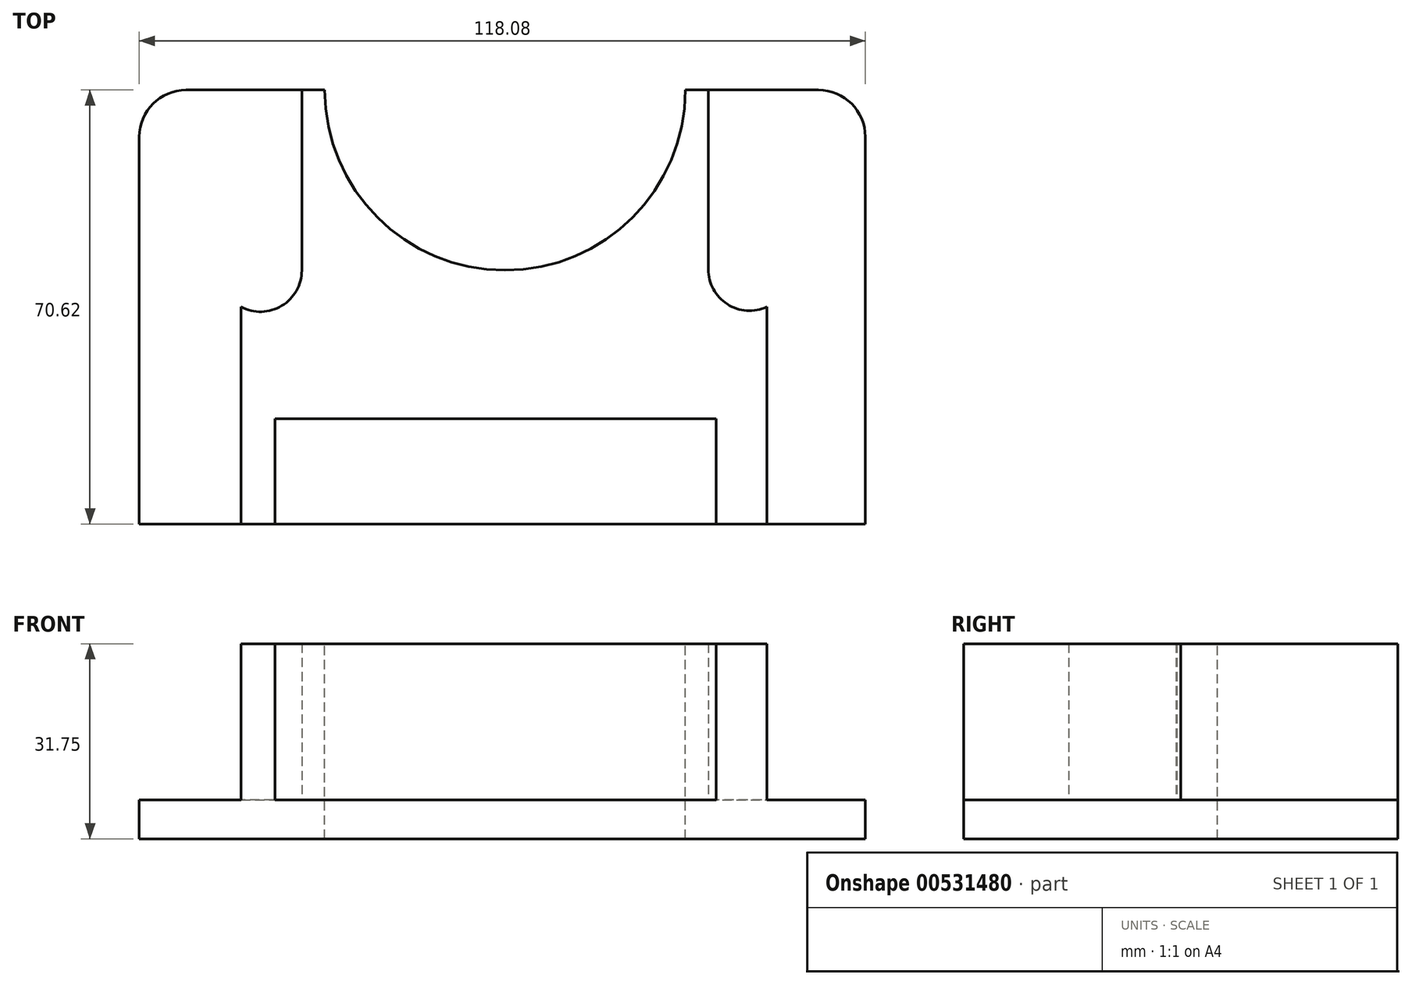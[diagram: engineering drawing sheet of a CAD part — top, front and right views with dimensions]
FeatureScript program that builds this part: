
annotation { "Feature Type Name" : "Feature", "Feature Type Description" : "" }
export const myFeature = defineFeature(function(context is Context, id is Id, definition is map)
    precondition{}
    {
        {
            var Q0;
            Q0=qCreatedBy(makeId("Top.planeOp"),FACE);
            var sketch = newSketch(context, id + "F0", { "sketchPlane" : qUnion([Q0])});
            skLineSegment(sketch, "E0.bottom", {"start": v(59.04, 35.31) * mm, "end": v(-59.04, 35.31) * mm});
            skLineSegment(sketch, "E0.top", {"start": v(59.04, -35.31) * mm, "end": v(-59.04, -35.31) * mm});
            skLineSegment(sketch, "E0.left", {"start": v(59.04, 35.31) * mm, "end": v(59.04, -35.31) * mm});
            skLineSegment(sketch, "E0.right", {"start": v(-59.04, 35.31) * mm, "end": v(-59.04, -35.31) * mm});
            skPoint(sketch, "E0.middle", {"position": v(0, 0) * mm});
            skSolve(sketch);
        }
        {
            var Q0;
            Q0=makeQuery(id+"F0.imprint","IMPRINT",FACE,{"disambiguationData":[TD([[makeQuery(id+"F0.imprint","IMPRINT",EDGE,{"derivedFrom":sQuery(id+"F0.wireOp",EDGE,"E0.bottom")}),1.0]])]});
            extrude(context, id + "F1", {"entities" : qUnion([Q0]), "depth" : 6.35 * mm, "offsetDistance" : 25.4 * mm});
        }
        {
            var Q0;
            Q0=makeQuery(id+"F1.opExtrude","SWEPT_EDGE",EDGE,{"disambiguationData":[OSD([sQuery(id+"F0.wireOp",EDGE,"E0.bottom"),sQuery(id+"F0.wireOp",EDGE,"E0.right")])]});
            var Q1;
            Q1=makeQuery(id+"F1.opExtrude","SWEPT_EDGE",EDGE,{"disambiguationData":[OSD([sQuery(id+"F0.wireOp",EDGE,"E0.bottom"),sQuery(id+"F0.wireOp",EDGE,"E0.left")])]});
            fillet(context, id + "F2", {"entities" : qUnion([Q0, Q1]), "radius" : 7.62 * mm, "tangentPropagation" : true, "allowEdgeOverflow" : false});
        }
        {
            var Q0;
            Q0=makeQuery(id+"F1.opExtrude","CAP_FACE",FACE,{"disambiguationData":[OSD([sQuery(id+"F0.wireOp",EDGE,"E0.bottom"),sQuery(id+"F0.wireOp",EDGE,"E0.top"),sQuery(id+"F0.wireOp",EDGE,"E0.left"),sQuery(id+"F0.wireOp",EDGE,"E0.right")])],"isStart":false});
            var sketch = newSketch(context, id + "F3", { "sketchPlane" : qUnion([Q0])});
            skLineSegment(sketch, "E1", {"start": v(-42.49, -35.31) * mm, "end": v(-36.97, -35.31) * mm});
            skLineSegment(sketch, "E2", {"start": v(-36.97, -35.31) * mm, "end": v(-36.97, -18.2) * mm});
            skLineSegment(sketch, "E3", {"start": v(-36.97, -18.2) * mm, "end": v(34.76, -18.2) * mm});
            skLineSegment(sketch, "E4", {"start": v(34.76, -18.2) * mm, "end": v(34.76, -35.31) * mm});
            skLineSegment(sketch, "E5", {"start": v(34.76, -35.31) * mm, "end": v(43.04, -35.31) * mm});
            skLineSegment(sketch, "E6", {"start": v(43.04, -35.31) * mm, "end": v(43.04, 0) * mm});
            skArc(sketch, "E7", {"start": v(33.51, 6.12) * mm, "mid": v(36.6, 0.46) * mm, "end": v(43.04, 0) * mm});
            skLineSegment(sketch, "E8", {"start": v(33.51, 6.12) * mm, "end": v(33.51, 35.31) * mm});
            skLineSegment(sketch, "E9", {"start": v(-42.49, -35.31) * mm, "end": v(-42.49, 0) * mm});
            skArc(sketch, "E10", {"start": v(-42.49, 0) * mm, "mid": v(-35.87, 0.19) * mm, "end": v(-32.62, 5.95) * mm});
            skLineSegment(sketch, "E11", {"start": v(-32.62, 5.95) * mm, "end": v(-32.62, 35.31) * mm});
            skLineSegment(sketch, "E12", {"start": v(-32.62, 35.31) * mm, "end": v(33.51, 35.31) * mm});
            skSolve(sketch);
        }
        {
            var Q0;
            Q0=makeQuery(id+"F3.imprint","IMPRINT",FACE,{"disambiguationData":[TD([[makeQuery(id+"F3.imprint","IMPRINT",EDGE,{"derivedFrom":sQuery(id+"F3.wireOp",EDGE,"E1")}),-1.0]])]});
            extrude(context, id + "F4", {"entities" : qUnion([Q0]), "operationType" : NewBodyOperationType.ADD, "depth" : 25.4 * mm, "offsetDistance" : 25.4 * mm});
        }
        {
            var Q0;
            Q0=makeQuery(id+"F4.opExtrude","CAP_FACE",FACE,{"disambiguationData":[OSD([sQuery(id+"F3.wireOp",EDGE,"E1"),sQuery(id+"F3.wireOp",EDGE,"E2"),sQuery(id+"F3.wireOp",EDGE,"E3"),sQuery(id+"F3.wireOp",EDGE,"E4"),sQuery(id+"F3.wireOp",EDGE,"E5"),sQuery(id+"F3.wireOp",EDGE,"E6"),sQuery(id+"F3.wireOp",EDGE,"E7"),sQuery(id+"F3.wireOp",EDGE,"E8"),sQuery(id+"F3.wireOp",EDGE,"E9"),sQuery(id+"F3.wireOp",EDGE,"E10"),sQuery(id+"F3.wireOp",EDGE,"E11"),sQuery(id+"F3.wireOp",EDGE,"E12")])],"isStart":false});
            var sketch = newSketch(context, id + "F5", { "sketchPlane" : qUnion([Q0])});
            skCircle(sketch, "E13", {"center": v(0.45, 35.31) * mm, "radius": 29.34 * mm});
            skSolve(sketch);
        }
        {
            var Q0;
            {var subQ0=sQuery(id+"F5.wireOp",EDGE,"E13");var subQ1=makeQuery(id+"F4.opExtrude","CAP_EDGE",EDGE,{"disambiguationData":[OSD([sQuery(id+"F3.wireOp",EDGE,"E12")])],"isStart":false});var subQ2=makeQuery(id+"F5.imprint","INTERSECT",VERTEX,{"disambiguationData":[OD(0.0)],"derivedFrom":[subQ1,subQ0]});Q0=makeQuery(id+"F5.imprint","IMPRINT",FACE,{"disambiguationData":[TD([[makeQuery(id+"F5.imprint","IMPRINT",EDGE,{"disambiguationData":[TD([[subQ2,1.0]])],"derivedFrom":subQ0}),1.0]])]});}
            extrude(context, id + "F6", {"entities" : qUnion([Q0]), "operationType" : NewBodyOperationType.REMOVE, "oppositeDirection" : true, "depth" : 50.8 * mm, "offsetDistance" : 25.4 * mm});
        }
    });
